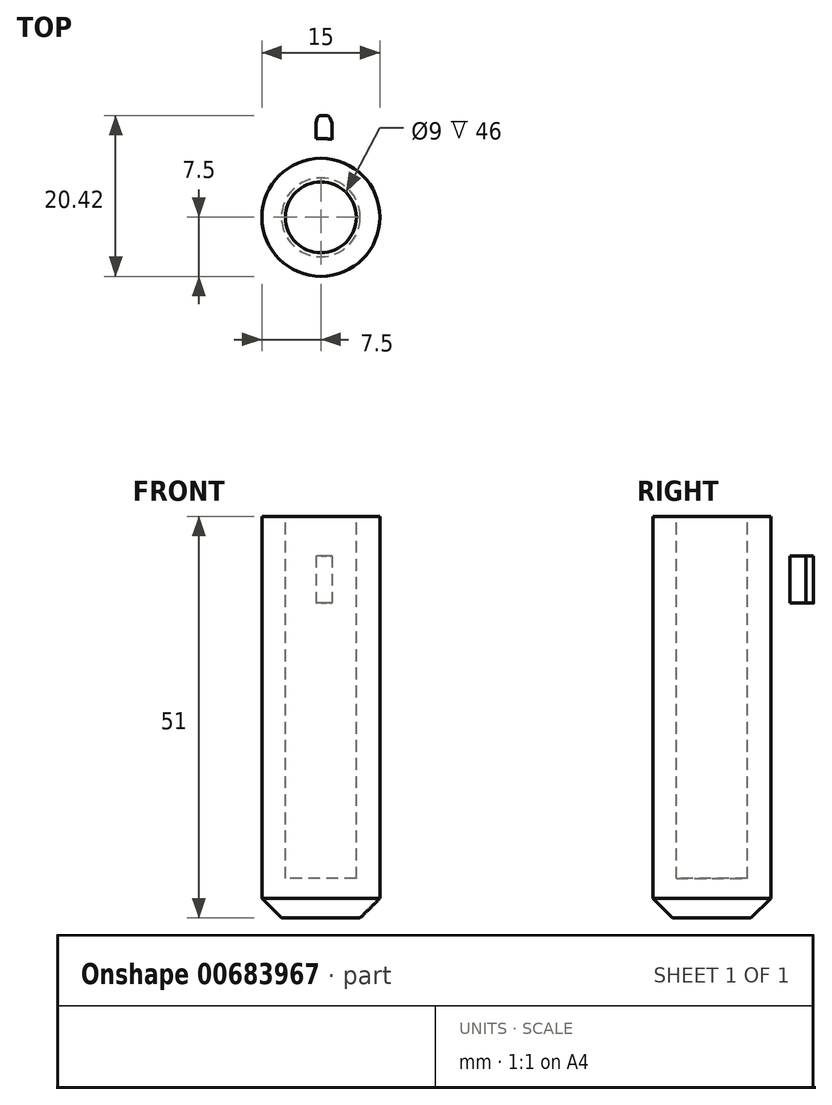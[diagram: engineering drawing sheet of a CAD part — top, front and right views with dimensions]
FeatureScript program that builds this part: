
annotation { "Feature Type Name" : "Feature", "Feature Type Description" : "" }
export const myFeature = defineFeature(function(context is Context, id is Id, definition is map)
    precondition{}
    {
        {
            var Q0;
            Q0=qCreatedBy(makeId("Top.planeOp"),FACE);
            var sketch = newSketch(context, id + "F0", { "sketchPlane" : qUnion([Q0])});
            skCircle(sketch, "E0", {"center": v(0, 0) * mm, "radius": 10 * mm});
            skLineSegment(sketch, "E1", {"start": v(-0.6, 9.98) * mm, "end": v(-0.6, 11.98) * mm});
            skLineSegment(sketch, "E2", {"start": v(-0.6, 11.98) * mm, "end": v(-0.46, 12.55) * mm});
            skLineSegment(sketch, "E3", {"start": v(0.03, 12.92) * mm, "end": v(0.7, 12.92) * mm});
            skLineSegment(sketch, "E4", {"start": v(1.17, 12.6) * mm, "end": v(1.4, 11.98) * mm});
            skLineSegment(sketch, "E5", {"start": v(1.4, 11.98) * mm, "end": v(1.4, 9.9) * mm});
            skPoint(sketch, "E6.visualSharp", {"position": v(-0.36, 12.92) * mm});
            skArc(sketch, "E6.filletArc", {"start": v(0.03, 12.92) * mm, "mid": v(-0.28, 12.82) * mm, "end": v(-0.46, 12.55) * mm});
            skPoint(sketch, "E7.visualSharp", {"position": v(1.05, 12.92) * mm});
            skArc(sketch, "E7.filletArc", {"start": v(1.17, 12.6) * mm, "mid": v(0.99, 12.83) * mm, "end": v(0.7, 12.92) * mm});
            skSolve(sketch);
        }
        {
            var Q0;
            {var subQ0=sQuery(id+"FQJoTvy09MMOVr5_0.12.F0.wireOp",EDGE,"E0");var subQ1=makeQuery(id+"FQJoTvy09MMOVr5_0.12.F0.imprint","INTERSECT",VERTEX,{"derivedFrom":[subQ0,sQuery(id+"FQJoTvy09MMOVr5_0.12.F0.wireOp",EDGE,"E1")]});Q0=makeQuery(id+"FQJoTvy09MMOVr5_0.12.F0.imprint","IMPRINT",FACE,{"disambiguationData":[TD([[makeQuery(id+"FQJoTvy09MMOVr5_0.12.F0.imprint","IMPRINT",EDGE,{"disambiguationData":[TD([[subQ1,1.0]])],"derivedFrom":subQ0}),1.0]])]});}
            var Q1;
            {var subQ0=sQuery(id+"FQJoTvy09MMOVr5_0.5.F0.wireOp",EDGE,"E1");Q1=makeQuery(id+"FQJoTvy09MMOVr5_0.5.F0.imprint","IMPRINT",FACE,{"disambiguationData":[TD([[makeQuery(id+"FQJoTvy09MMOVr5_0.5.F0.imprint","IMPRINT",EDGE,{"derivedFrom":subQ0}),-1.0]])]});}
            var Q2;
            {var subQ0=sQuery(id+"FQJoTvy09MMOVr5_0.4.F0.wireOp",EDGE,"E1");Q2=makeQuery(id+"FQJoTvy09MMOVr5_0.4.F0.imprint","IMPRINT",FACE,{"disambiguationData":[TD([[makeQuery(id+"FQJoTvy09MMOVr5_0.4.F0.imprint","IMPRINT",EDGE,{"derivedFrom":subQ0}),-1.0]])]});}
            var Q3;
            {var subQ0=sQuery(id+"FQJoTvy09MMOVr5_0.3.F0.wireOp",EDGE,"E1");Q3=makeQuery(id+"FQJoTvy09MMOVr5_0.3.F0.imprint","IMPRINT",FACE,{"disambiguationData":[TD([[makeQuery(id+"FQJoTvy09MMOVr5_0.3.F0.imprint","IMPRINT",EDGE,{"derivedFrom":subQ0}),-1.0]])]});}
            var Q4;
            {var subQ0=sQuery(id+"FQJoTvy09MMOVr5_0.2.F0.wireOp",EDGE,"E1");Q4=makeQuery(id+"FQJoTvy09MMOVr5_0.2.F0.imprint","IMPRINT",FACE,{"disambiguationData":[TD([[makeQuery(id+"FQJoTvy09MMOVr5_0.2.F0.imprint","IMPRINT",EDGE,{"derivedFrom":subQ0}),-1.0]])]});}
            var Q5;
            {var subQ0=sQuery(id+"FQJoTvy09MMOVr5_0.1.F0.wireOp",EDGE,"E1");Q5=makeQuery(id+"FQJoTvy09MMOVr5_0.1.F0.imprint","IMPRINT",FACE,{"disambiguationData":[TD([[makeQuery(id+"FQJoTvy09MMOVr5_0.1.F0.imprint","IMPRINT",EDGE,{"derivedFrom":subQ0}),-1.0]])]});}
            var Q6;
            {var subQ0=sQuery(id+"F0.wireOp",EDGE,"E1");Q6=makeQuery(id+"F0.imprint","IMPRINT",FACE,{"disambiguationData":[TD([[makeQuery(id+"F0.imprint","IMPRINT",EDGE,{"derivedFrom":subQ0}),-1.0]])]});}
            var Q7;
            {var subQ0=sQuery(id+"FQJoTvy09MMOVr5_0.19.F0.wireOp",EDGE,"E1");Q7=makeQuery(id+"FQJoTvy09MMOVr5_0.19.F0.imprint","IMPRINT",FACE,{"disambiguationData":[TD([[makeQuery(id+"FQJoTvy09MMOVr5_0.19.F0.imprint","IMPRINT",EDGE,{"derivedFrom":subQ0}),-1.0]])]});}
            var Q8;
            {var subQ0=sQuery(id+"FQJoTvy09MMOVr5_0.18.F0.wireOp",EDGE,"E1");Q8=makeQuery(id+"FQJoTvy09MMOVr5_0.18.F0.imprint","IMPRINT",FACE,{"disambiguationData":[TD([[makeQuery(id+"FQJoTvy09MMOVr5_0.18.F0.imprint","IMPRINT",EDGE,{"derivedFrom":subQ0}),-1.0]])]});}
            var Q9;
            {var subQ0=sQuery(id+"FQJoTvy09MMOVr5_0.17.F0.wireOp",EDGE,"E1");Q9=makeQuery(id+"FQJoTvy09MMOVr5_0.17.F0.imprint","IMPRINT",FACE,{"disambiguationData":[TD([[makeQuery(id+"FQJoTvy09MMOVr5_0.17.F0.imprint","IMPRINT",EDGE,{"derivedFrom":subQ0}),-1.0]])]});}
            var Q10;
            {var subQ0=sQuery(id+"FQJoTvy09MMOVr5_0.16.F0.wireOp",EDGE,"E1");Q10=makeQuery(id+"FQJoTvy09MMOVr5_0.16.F0.imprint","IMPRINT",FACE,{"disambiguationData":[TD([[makeQuery(id+"FQJoTvy09MMOVr5_0.16.F0.imprint","IMPRINT",EDGE,{"derivedFrom":subQ0}),-1.0]])]});}
            var Q11;
            {var subQ0=sQuery(id+"FQJoTvy09MMOVr5_0.15.F0.wireOp",EDGE,"E1");Q11=makeQuery(id+"FQJoTvy09MMOVr5_0.15.F0.imprint","IMPRINT",FACE,{"disambiguationData":[TD([[makeQuery(id+"FQJoTvy09MMOVr5_0.15.F0.imprint","IMPRINT",EDGE,{"derivedFrom":subQ0}),-1.0]])]});}
            var Q12;
            {var subQ0=sQuery(id+"FQJoTvy09MMOVr5_0.14.F0.wireOp",EDGE,"E1");Q12=makeQuery(id+"FQJoTvy09MMOVr5_0.14.F0.imprint","IMPRINT",FACE,{"disambiguationData":[TD([[makeQuery(id+"FQJoTvy09MMOVr5_0.14.F0.imprint","IMPRINT",EDGE,{"derivedFrom":subQ0}),-1.0]])]});}
            var Q13;
            {var subQ0=sQuery(id+"FQJoTvy09MMOVr5_0.13.F0.wireOp",EDGE,"E1");Q13=makeQuery(id+"FQJoTvy09MMOVr5_0.13.F0.imprint","IMPRINT",FACE,{"disambiguationData":[TD([[makeQuery(id+"FQJoTvy09MMOVr5_0.13.F0.imprint","IMPRINT",EDGE,{"derivedFrom":subQ0}),-1.0]])]});}
            var Q14;
            {var subQ0=sQuery(id+"FQJoTvy09MMOVr5_0.12.F0.wireOp",EDGE,"E1");Q14=makeQuery(id+"FQJoTvy09MMOVr5_0.12.F0.imprint","IMPRINT",FACE,{"disambiguationData":[TD([[makeQuery(id+"FQJoTvy09MMOVr5_0.12.F0.imprint","IMPRINT",EDGE,{"derivedFrom":subQ0}),-1.0]])]});}
            var Q15;
            {var subQ0=sQuery(id+"FQJoTvy09MMOVr5_0.11.F0.wireOp",EDGE,"E1");Q15=makeQuery(id+"FQJoTvy09MMOVr5_0.11.F0.imprint","IMPRINT",FACE,{"disambiguationData":[TD([[makeQuery(id+"FQJoTvy09MMOVr5_0.11.F0.imprint","IMPRINT",EDGE,{"derivedFrom":subQ0}),-1.0]])]});}
            var Q16;
            {var subQ0=sQuery(id+"FQJoTvy09MMOVr5_0.10.F0.wireOp",EDGE,"E1");Q16=makeQuery(id+"FQJoTvy09MMOVr5_0.10.F0.imprint","IMPRINT",FACE,{"disambiguationData":[TD([[makeQuery(id+"FQJoTvy09MMOVr5_0.10.F0.imprint","IMPRINT",EDGE,{"derivedFrom":subQ0}),-1.0]])]});}
            var Q17;
            {var subQ0=sQuery(id+"FQJoTvy09MMOVr5_0.9.F0.wireOp",EDGE,"E1");Q17=makeQuery(id+"FQJoTvy09MMOVr5_0.9.F0.imprint","IMPRINT",FACE,{"disambiguationData":[TD([[makeQuery(id+"FQJoTvy09MMOVr5_0.9.F0.imprint","IMPRINT",EDGE,{"derivedFrom":subQ0}),-1.0]])]});}
            var Q18;
            {var subQ0=sQuery(id+"FQJoTvy09MMOVr5_0.6.F0.wireOp",EDGE,"E1");Q18=makeQuery(id+"FQJoTvy09MMOVr5_0.6.F0.imprint","IMPRINT",FACE,{"disambiguationData":[TD([[makeQuery(id+"FQJoTvy09MMOVr5_0.6.F0.imprint","IMPRINT",EDGE,{"derivedFrom":subQ0}),-1.0]])]});}
            var Q19;
            {var subQ0=sQuery(id+"FQJoTvy09MMOVr5_0.7.F0.wireOp",EDGE,"E1");Q19=makeQuery(id+"FQJoTvy09MMOVr5_0.7.F0.imprint","IMPRINT",FACE,{"disambiguationData":[TD([[makeQuery(id+"FQJoTvy09MMOVr5_0.7.F0.imprint","IMPRINT",EDGE,{"derivedFrom":subQ0}),-1.0]])]});}
            var Q20;
            {var subQ0=sQuery(id+"FQJoTvy09MMOVr5_0.8.F0.wireOp",EDGE,"E1");Q20=makeQuery(id+"FQJoTvy09MMOVr5_0.8.F0.imprint","IMPRINT",FACE,{"disambiguationData":[TD([[makeQuery(id+"FQJoTvy09MMOVr5_0.8.F0.imprint","IMPRINT",EDGE,{"derivedFrom":subQ0}),-1.0]])]});}
            extrude(context, id + "F1", {"entities" : qUnion([Q0, Q1, Q2, Q3, Q4, Q5, Q6, Q7, Q8, Q9, Q10, Q11, Q12, Q13, Q14, Q15, Q16, Q17, Q18, Q19, Q20]), "depth" : 6 * mm, "offsetDistance" : 25 * mm});
        }
        {
            var Q0;
            Q0=qCreatedBy(makeId("Top.planeOp"),FACE);
            var sketch = newSketch(context, id + "F2", { "sketchPlane" : qUnion([Q0])});
            skCircle(sketch, "E8", {"center": v(0, 0) * mm, "radius": 7.5 * mm});
            skSolve(sketch);
        }
        {
            var Q0;
            Q0 = qSketchRegion(id + "F2", true);
            extrude(context, id + "F3", {"entities" : qUnion([Q0]), "operationType" : NewBodyOperationType.ADD, "oppositeDirection" : true, "depth" : 40 * mm, "offsetDistance" : 25 * mm, "hasSecondDirection" : true, "secondDirectionOppositeDirection" : false, "secondDirectionDepth" : 11 * mm});
        }
        {
            var Q0;
            Q0=makeQuery(id+"F3.opExtrude","CAP_EDGE",EDGE,{"disambiguationData":[OSD([sQuery(id+"F2.wireOp",EDGE,"E8")])],"isStart":false});
            var Q1;
            Q1=makeQuery(id+"F3.opExtrude","CAP_FACE",FACE,{"disambiguationData":[OSD([sQuery(id+"F2.wireOp",EDGE,"E8")])],"isStart":false});
            chamfer(context, id + "F4", {"entities" : qUnion([Q0, Q1]), "chamferType" : ChamferType.OFFSET_ANGLE, "width" : 2.5 * mm, "oppositeDirection" : false, "angle" : 45 * degree, "tangentPropagation" : true});
        }
        {
            var Q0;
            Q0=qCreatedBy(makeId("Top.planeOp"),FACE);
            var sketch = newSketch(context, id + "F5", { "sketchPlane" : qUnion([Q0])});
            skCircle(sketch, "E9", {"center": v(0, 0) * mm, "radius": 4.5 * mm});
            skSolve(sketch);
        }
        {
            var Q0;
            Q0 = qSketchRegion(id + "F5", true);
            extrude(context, id + "F6", {"entities" : qUnion([Q0]), "operationType" : NewBodyOperationType.REMOVE, "oppositeDirection" : true, "depth" : 35 * mm, "offsetDistance" : 25 * mm, "hasSecondDirection" : true, "secondDirectionOppositeDirection" : false, "secondDirectionDepth" : 11 * mm});
        }
    });
